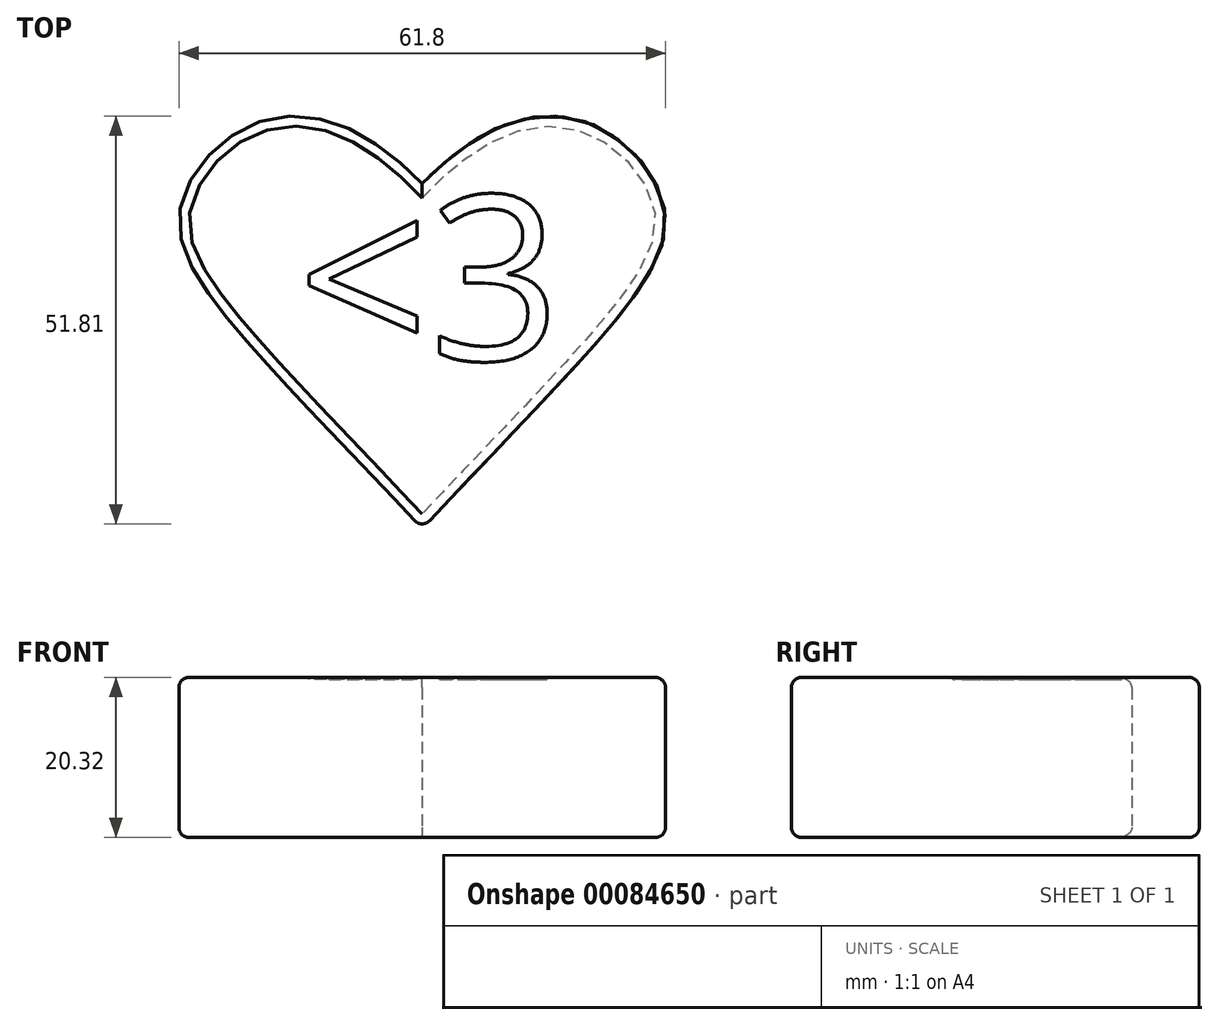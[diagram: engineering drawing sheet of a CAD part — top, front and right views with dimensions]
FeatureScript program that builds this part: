
annotation { "Feature Type Name" : "Feature", "Feature Type Description" : "" }
export const myFeature = defineFeature(function(context is Context, id is Id, definition is map)
    precondition{}
    {
        {
            var Q0;
            Q0=qCreatedBy(makeId("Top.planeOp"),FACE);
            var sketch = newSketch(context, id + "F0", { "sketchPlane" : qUnion([Q0])});
            skFitSpline(sketch, "E0", {"points": [v(0, 0) * mm, v(-29.63, 0) * mm, v(0, -43.83) * mm], "startDerivative": vector(-102.75, 106.03) * mm, "endDerivative": vector(134.16, -142.35) * mm});
            skLineSegment(sketch, "E1", {"start": v(0, 0) * mm, "end": v(0, -43.83) * mm});
            skSolve(sketch);
        }
        {
            var Q0;
            Q0 = qSketchRegion(id + "F0", true);
            extrude(context, id + "F1", {"entities" : qUnion([Q0]), "depth" : 20.32 * mm});
        }
        {
            var Q0;
            Q0=makeQuery(id+"F1.opExtrude","SWEPT_BODY",BODY,{"disambiguationData":[OSD([sQuery(id+"F0.wireOp",EDGE,"E0"),sQuery(id+"F0.wireOp",EDGE,"E1")])]});
            var Q1;
            Q1=qCreatedBy(makeId("Right.planeOp"),FACE);
            mirror(context, id + "F2", {"operationType" : NewBodyOperationType.ADD, "entities" : qUnion([Q0]), "mirrorPlane" : qUnion([Q1])});
        }
        {
            var Q0;
            {var subQ0=makeQuery(id+"F1.opExtrude","CAP_FACE",FACE,{"disambiguationData":[OSD([sQuery(id+"F0.wireOp",EDGE,"E0"),sQuery(id+"F0.wireOp",EDGE,"E1")])],"isStart":false});Q0=makeQuery(id+"F2.boolean.opBoolean","MERGE",FACE,{"derivedFrom":[subQ0,makeQuery(id+"F2.opPattern","COPY",FACE,{"derivedFrom":subQ0,"instanceName":"1"})]});}
            var sketch = newSketch(context, id + "F3", { "sketchPlane" : qUnion([Q0])});
            skText(sketch, "E2", { "text": "<3", "fontName": "OpenSans-Regular.ttf"});
            const initialGuessF3  = {"E2": [-0.01588, -0.02243, 1, 0, 0.02107]};
            skSetInitialGuess(sketch, initialGuessF3);
            skSolve(sketch);
        }
        {
            var Q0;
            Q0 = qSketchRegion(id + "F3", true);
            extrude(context, id + "F4", {"entities" : qUnion([Q0]), "operationType" : NewBodyOperationType.REMOVE, "oppositeDirection" : true, "depth" : 0.25 * mm});
        }
        {
            var Q0;
            Q0=makeQuery(id+"F1.opExtrude","CAP_EDGE",EDGE,{"disambiguationData":[OSD([sQuery(id+"F0.wireOp",EDGE,"E0")])],"isStart":false});
            var Q1;
            Q1=makeQuery(id+"F2.opPattern","COPY",EDGE,{"derivedFrom":makeQuery(id+"F1.opExtrude","CAP_EDGE",EDGE,{"disambiguationData":[OSD([sQuery(id+"F0.wireOp",EDGE,"E0")])],"isStart":false}),"instanceName":"1"});
            var Q2;
            Q2=makeQuery(id+"F2.opPattern","COPY",EDGE,{"derivedFrom":makeQuery(id+"F1.opExtrude","CAP_EDGE",EDGE,{"disambiguationData":[OSD([sQuery(id+"F0.wireOp",EDGE,"E0")])],"isStart":true}),"instanceName":"1"});
            var Q3;
            {var subQ0=sQuery(id+"F0.wireOp",EDGE,"E1");var subQ1=sQuery(id+"F0.wireOp",EDGE,"E0");var subQ2=makeQuery(id+"F1.opExtrude","SWEPT_EDGE",EDGE,{"disambiguationData":[OSD([subQ1,subQ0]),TDD([makeQuery(id+"F0.imprint","INTERSECT",VERTEX,{"disambiguationData":[OD(1.0)],"derivedFrom":[subQ1,subQ0]})])]});Q3=makeQuery(id+"F2.boolean.opBoolean","MERGE",EDGE,{"derivedFrom":[subQ2,makeQuery(id+"F2.opPattern","COPY",EDGE,{"derivedFrom":subQ2,"instanceName":"1"})]});}
            var Q4;
            Q4=makeQuery(id+"F1.opExtrude","CAP_EDGE",EDGE,{"disambiguationData":[OSD([sQuery(id+"F0.wireOp",EDGE,"E0")])],"isStart":true});
            fillet(context, id + "F5", {"entities" : qUnion([Q0, Q1, Q2, Q3, Q4]), "radius" : 1.27 * mm, "tangentPropagation" : true, "allowEdgeOverflow" : false});
        }
    });
